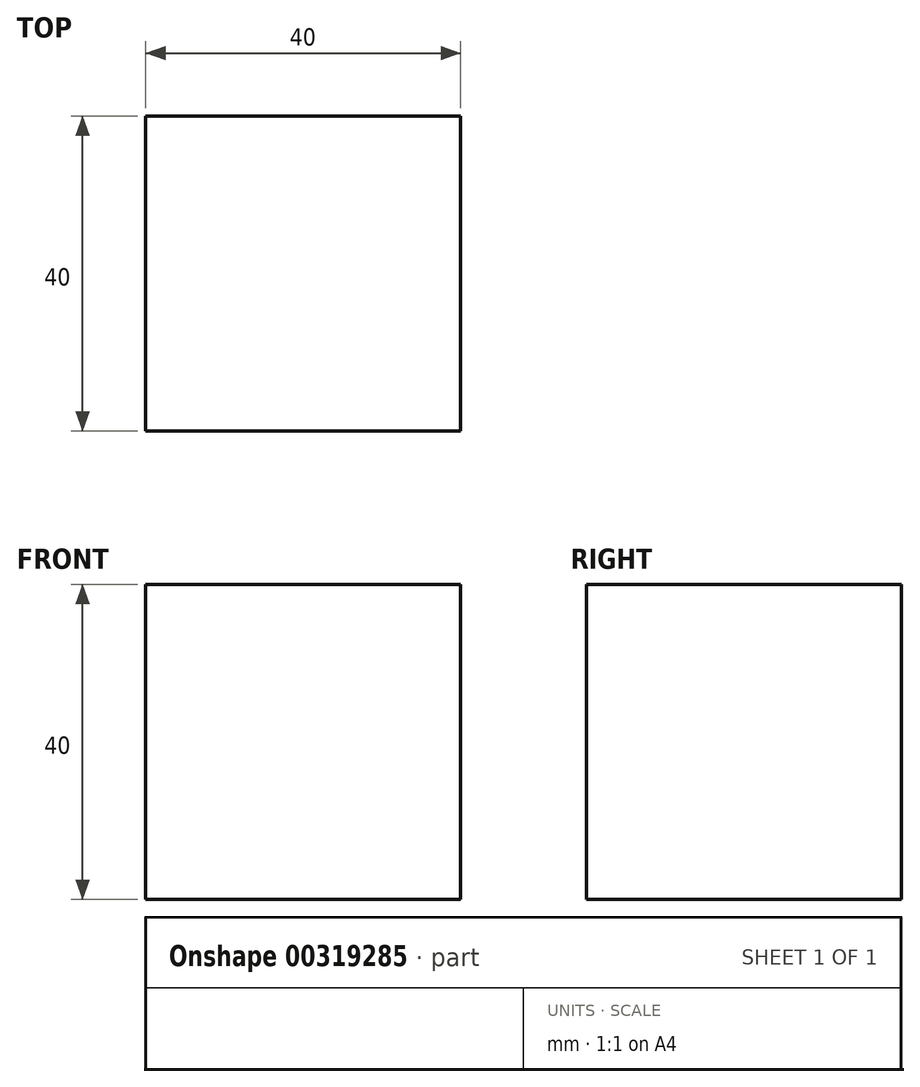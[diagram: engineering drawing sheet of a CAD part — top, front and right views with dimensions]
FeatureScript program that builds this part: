
annotation { "Feature Type Name" : "Feature", "Feature Type Description" : "" }
export const myFeature = defineFeature(function(context is Context, id is Id, definition is map)
    precondition{}
    {
        {
            var Q0;
            Q0=qCreatedBy(makeId("Front.planeOp"),FACE);
            var sketch = newSketch(context, id + "F0", { "sketchPlane" : qUnion([Q0])});
            skLineSegment(sketch, "E0.bottom", {"start": v(0, 0) * mm, "end": v(40, 0) * mm});
            skLineSegment(sketch, "E0.top", {"start": v(0, -40) * mm, "end": v(40, -40) * mm});
            skLineSegment(sketch, "E0.left", {"start": v(0, 0) * mm, "end": v(0, -40) * mm});
            skLineSegment(sketch, "E0.right", {"start": v(40, 0) * mm, "end": v(40, -40) * mm});
            skSolve(sketch);
        }
        {
            var Q0;
            Q0 = qSketchRegion(id + "F0", true);
            extrude(context, id + "F1", {"entities" : qUnion([Q0]), "depth" : 40 * mm});
        }
    });
